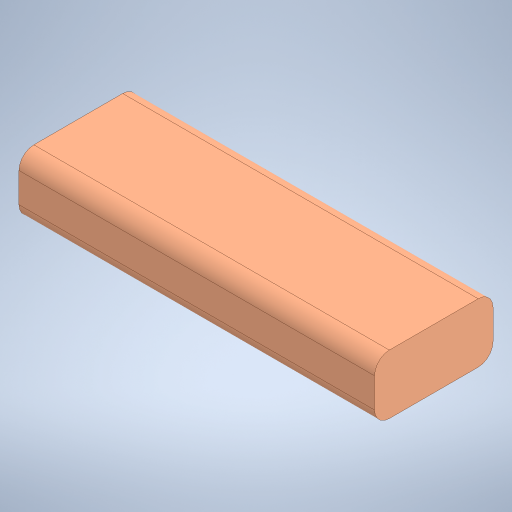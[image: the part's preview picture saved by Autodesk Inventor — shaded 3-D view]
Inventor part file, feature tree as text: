
AUTODESK INVENTOR PART (.ipt)
format: ipt  version: 2024 (Build 280153000, 153)  size: 226,304 bytes
history: native  units: mm
features: extrude x1
ambient origin geometry x8: Origin, YZ Plane, XZ Plane, XY Plane, X Axis, Y Axis, Z Axis, Center Point
bodies: Solid1 (feature_tree)
feature tree (1):
  extrude  "Extrusion1"  Depth=101.6mm
